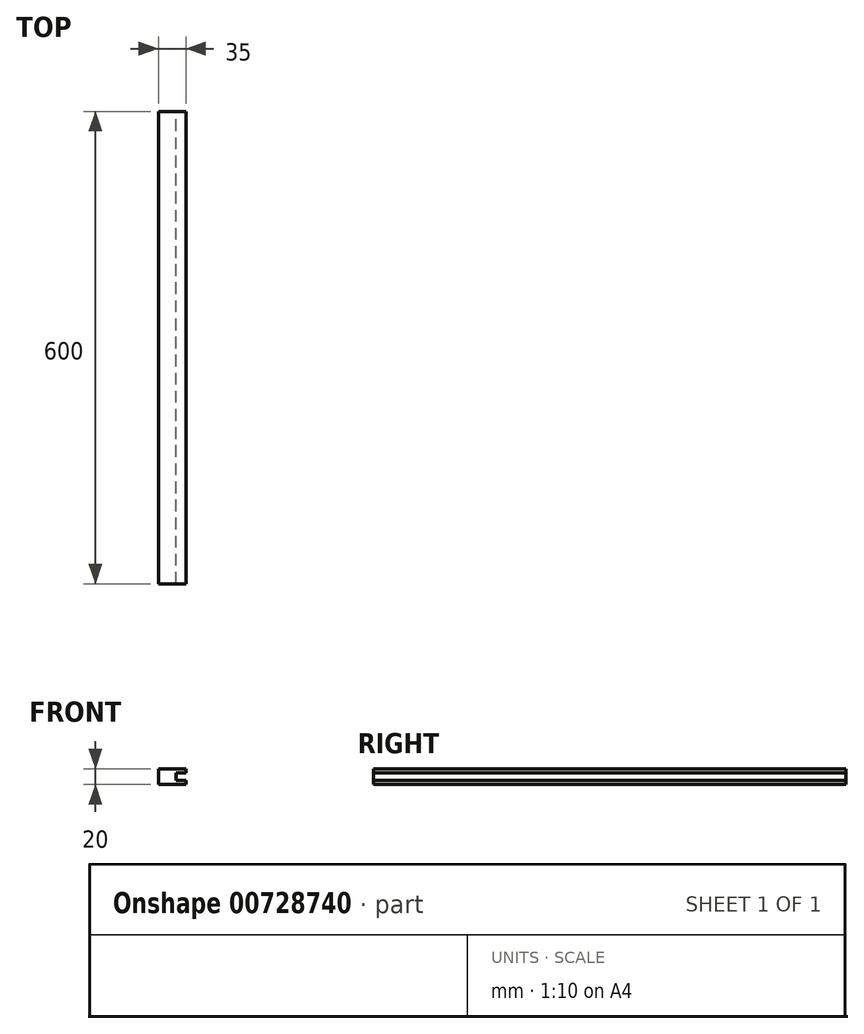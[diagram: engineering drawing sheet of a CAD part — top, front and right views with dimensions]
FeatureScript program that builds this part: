
annotation { "Feature Type Name" : "Feature", "Feature Type Description" : "" }
export const myFeature = defineFeature(function(context is Context, id is Id, definition is map)
    precondition{}
    {
        {
            var Q0;
            Q0=qCreatedBy(makeId("Front.planeOp"),FACE);
            var sketch = newSketch(context, id + "F0", { "sketchPlane" : qUnion([Q0])});
            skLineSegment(sketch, "E0", {"start": v(0.51, 0) * mm, "end": v(0.51, 10) * mm});
            skLineSegment(sketch, "E1", {"start": v(0.51, 10) * mm, "end": v(35.51, 10) * mm});
            skLineSegment(sketch, "E2", {"start": v(35.51, 10) * mm, "end": v(35.51, 5) * mm});
            skLineSegment(sketch, "E3", {"start": v(35.51, 5) * mm, "end": v(22.75, 5) * mm});
            skLineSegment(sketch, "E4", {"start": v(22.75, 5) * mm, "end": v(22.75, 0) * mm});
            skLineSegment(sketch, "E5", {"start": v(0.51, -10) * mm, "end": v(0.51, 0) * mm});
            skLineSegment(sketch, "E6", {"start": v(35.51, -10) * mm, "end": v(0.51, -10) * mm});
            skLineSegment(sketch, "E7", {"start": v(35.51, -5) * mm, "end": v(35.51, -10) * mm});
            skLineSegment(sketch, "E8", {"start": v(22.75, -5) * mm, "end": v(35.51, -5) * mm});
            skLineSegment(sketch, "E9", {"start": v(22.75, -5) * mm, "end": v(22.75, 0) * mm});
            skSolve(sketch);
        }
        {
            var Q0;
            Q0=makeQuery(id+"F0.imprint","IMPRINT",FACE,{"disambiguationData":[TD([[makeQuery(id+"F0.imprint","IMPRINT",EDGE,{"derivedFrom":sQuery(id+"F0.wireOp",EDGE,"E0")}),-1.0]])]});
            extrude(context, id + "F1", {"entities" : qUnion([Q0]), "depth" : 600 * mm, "offsetDistance" : 25 * mm});
        }
    });
